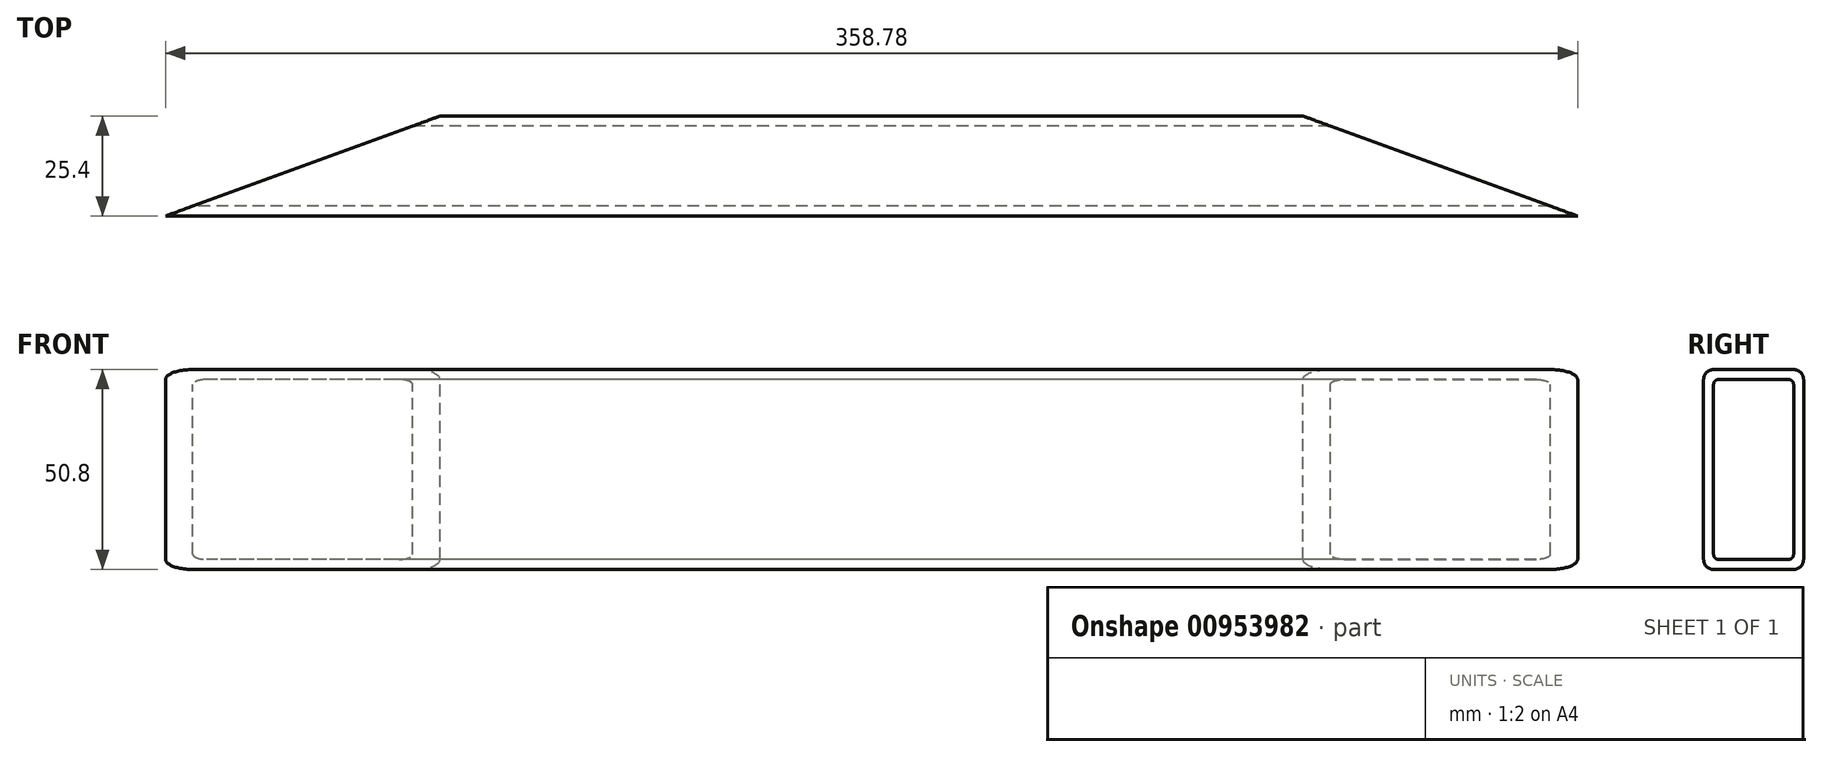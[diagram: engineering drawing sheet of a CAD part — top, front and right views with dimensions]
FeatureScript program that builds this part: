
annotation { "Feature Type Name" : "Feature", "Feature Type Description" : "" }
export const myFeature = defineFeature(function(context is Context, id is Id, definition is map)
    precondition{}
    {
        {
            var Q0;
            Q0=qCreatedBy(makeId("Front.planeOp"),FACE);
            var sketch = newSketch(context, id + "F0", { "sketchPlane" : qUnion([Q0])});
            skLineSegment(sketch, "E0.bottom", {"start": v(179.39, -25.4) * mm, "end": v(-179.39, -25.4) * mm});
            skLineSegment(sketch, "E0.top", {"start": v(179.39, 25.4) * mm, "end": v(-179.39, 25.4) * mm});
            skLineSegment(sketch, "E0.left", {"start": v(179.39, -25.4) * mm, "end": v(179.39, 25.4) * mm});
            skLineSegment(sketch, "E0.right", {"start": v(-179.39, -25.4) * mm, "end": v(-179.39, 25.4) * mm});
            skPoint(sketch, "E0.middle", {"position": v(0, 0) * mm});
            skSolve(sketch);
        }
        {
            var Q0;
            Q0=makeQuery(id+"F0.imprint","IMPRINT",FACE,{"disambiguationData":[TD([[makeQuery(id+"F0.imprint","IMPRINT",EDGE,{"derivedFrom":sQuery(id+"F0.wireOp",EDGE,"E0.bottom")}),-1.0]])]});
            extrude(context, id + "F1", {"entities" : qUnion([Q0]), "endBound" : BoundingType.SYMMETRIC, "depth" : 25.4 * mm, "offsetDistance" : 25.4 * mm});
        }
        {
            var Q0;
            Q0=makeQuery(id+"F1.opExtrude","SWEPT_FACE",FACE,{"disambiguationData":[OSD([sQuery(id+"F0.wireOp",EDGE,"E0.right")])]});
            var Q1;
            Q1=makeQuery(id+"F1.opExtrude","SWEPT_FACE",FACE,{"disambiguationData":[OSD([sQuery(id+"F0.wireOp",EDGE,"E0.left")])]});
            shell(context, id + "F2", {"entities" : qUnion([Q0, Q1]), "thickness" : 2.54 * mm});
        }
        {
            var Q0;
            Q0=makeQuery(id+"F1.opExtrude","SWEPT_FACE",FACE,{"disambiguationData":[OSD([sQuery(id+"F0.wireOp",EDGE,"E0.top")])]});
            var sketch = newSketch(context, id + "F3", { "sketchPlane" : qUnion([Q0])});
            skLineSegment(sketch, "E1", {"start": v(-179.39, -12.7) * mm, "end": v(-109.6, 12.7) * mm});
            skLineSegment(sketch, "E2", {"start": v(-109.6, 12.7) * mm, "end": v(-179.39, 12.7) * mm});
            skLineSegment(sketch, "E3", {"start": v(-179.39, 12.7) * mm, "end": v(-179.39, -12.7) * mm});
            skLineSegment(sketch, "E4.MirrorCS", {"start": v(179.39, -12.7) * mm, "end": v(109.6, 12.7) * mm});
            skLineSegment(sketch, "E5.MirrorCS", {"start": v(109.6, 12.7) * mm, "end": v(179.39, 12.7) * mm});
            skLineSegment(sketch, "E6.MirrorCS", {"start": v(179.39, 12.7) * mm, "end": v(179.39, -12.7) * mm});
            skSolve(sketch);
        }
        {
            var Q0;
            Q0=makeQuery(id+"F3.imprint","IMPRINT",FACE,{"disambiguationData":[TD([[makeQuery(id+"F3.imprint","IMPRINT",EDGE,{"derivedFrom":sQuery(id+"F3.wireOp",EDGE,"E1")}),1.0]])]});
            var Q1;
            Q1=makeQuery(id+"F3.imprint","IMPRINT",FACE,{"disambiguationData":[TD([[makeQuery(id+"F3.imprint","IMPRINT",EDGE,{"derivedFrom":sQuery(id+"F3.wireOp",EDGE,"E4.MirrorCS")}),-1.0]])]});
            extrude(context, id + "F4", {"entities" : qUnion([Q0, Q1]), "operationType" : NewBodyOperationType.REMOVE, "endBound" : BoundingType.THROUGH_ALL, "oppositeDirection" : true, "depth" : 25.4 * mm, "offsetDistance" : 25.4 * mm});
        }
        {
            var Q0;
            Q0=makeQuery(id+"F1.opExtrude","CAP_EDGE",EDGE,{"disambiguationData":[OSD([sQuery(id+"F0.wireOp",EDGE,"E0.top")])],"isStart":false});
            var Q1;
            Q1=makeQuery(id+"F1.opExtrude","CAP_EDGE",EDGE,{"disambiguationData":[OSD([sQuery(id+"F0.wireOp",EDGE,"E0.top")])],"isStart":true});
            var Q2;
            Q2=makeQuery(id+"F1.opExtrude","CAP_EDGE",EDGE,{"disambiguationData":[OSD([sQuery(id+"F0.wireOp",EDGE,"E0.bottom")])],"isStart":true});
            var Q3;
            Q3=makeQuery(id+"F1.opExtrude","CAP_EDGE",EDGE,{"disambiguationData":[OSD([sQuery(id+"F0.wireOp",EDGE,"E0.bottom")])],"isStart":false});
            fillet(context, id + "F5", {"entities" : qUnion([Q0, Q1, Q2, Q3]), "radius" : 2.54 * mm, "tangentPropagation" : true, "allowEdgeOverflow" : false});
        }
        {
            var Q0;
            {var subQ0=sQuery(id+"F0.wireOp",EDGE,"E0.bottom");Q0=makeQuery(id+"F2.opShell","OFFSET_EDGE",EDGE,{"disambiguationData":[OSD([subQ0]),TDD([makeQuery(id+"F1.opExtrude","CAP_EDGE",EDGE,{"disambiguationData":[OSD([subQ0])],"isStart":false})])]});}
            var Q1;
            {var subQ0=sQuery(id+"F0.wireOp",EDGE,"E0.top");Q1=makeQuery(id+"F2.opShell","OFFSET_EDGE",EDGE,{"disambiguationData":[OSD([subQ0]),TDD([makeQuery(id+"F1.opExtrude","CAP_EDGE",EDGE,{"disambiguationData":[OSD([subQ0])],"isStart":false})])]});}
            var Q2;
            {var subQ0=sQuery(id+"F0.wireOp",EDGE,"E0.top");Q2=makeQuery(id+"F2.opShell","OFFSET_EDGE",EDGE,{"disambiguationData":[OSD([subQ0]),TDD([makeQuery(id+"F1.opExtrude","CAP_EDGE",EDGE,{"disambiguationData":[OSD([subQ0])],"isStart":true})])]});}
            var Q3;
            {var subQ0=sQuery(id+"F0.wireOp",EDGE,"E0.bottom");Q3=makeQuery(id+"F2.opShell","OFFSET_EDGE",EDGE,{"disambiguationData":[OSD([subQ0]),TDD([makeQuery(id+"F1.opExtrude","CAP_EDGE",EDGE,{"disambiguationData":[OSD([subQ0])],"isStart":true})])]});}
            fillet(context, id + "F6", {"entities" : qUnion([Q0, Q1, Q2, Q3]), "radius" : 1.27 * mm, "tangentPropagation" : true, "allowEdgeOverflow" : false});
        }
    });
